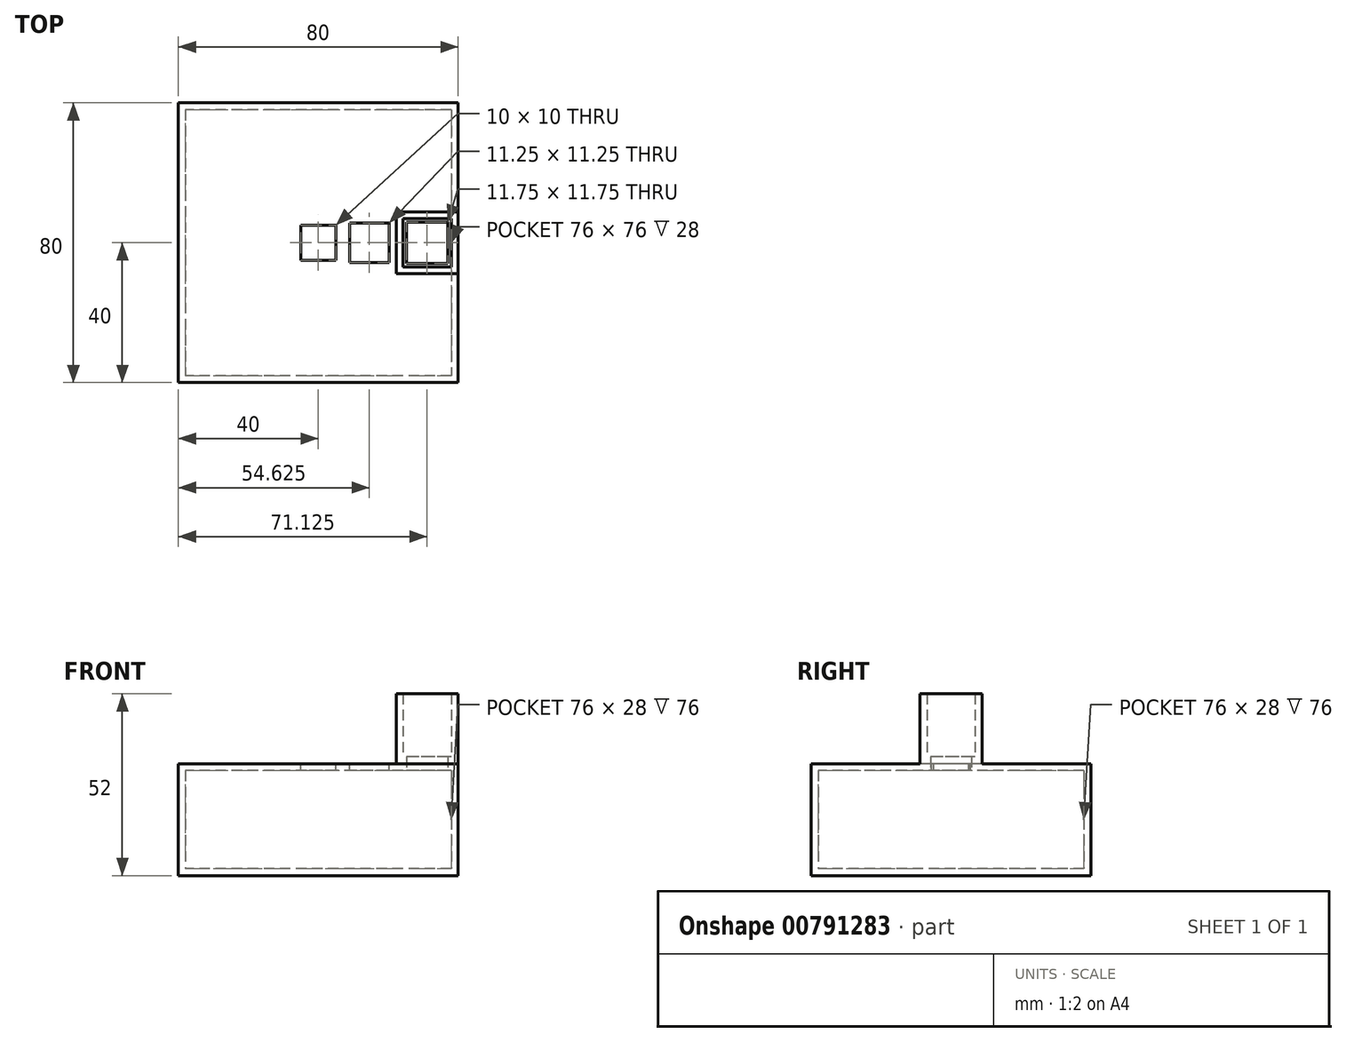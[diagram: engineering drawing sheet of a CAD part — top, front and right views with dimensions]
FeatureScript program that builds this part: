
annotation { "Feature Type Name" : "Feature", "Feature Type Description" : "" }
export const myFeature = defineFeature(function(context is Context, id is Id, definition is map)
    precondition{}
    {
        {
            var Q0;
            Q0=qCreatedBy(makeId("Top.planeOp"),FACE);
            var sketch = newSketch(context, id + "F0", { "sketchPlane" : qUnion([Q0])});
            skLineSegment(sketch, "E0.bottom", {"start": v(38, 38) * mm, "end": v(-38, 38) * mm});
            skLineSegment(sketch, "E0.top", {"start": v(38, -38) * mm, "end": v(-38, -38) * mm});
            skLineSegment(sketch, "E0.left", {"start": v(38, 38) * mm, "end": v(38, -38) * mm});
            skLineSegment(sketch, "E0.right", {"start": v(-38, 38) * mm, "end": v(-38, -38) * mm});
            skPoint(sketch, "E0.middle", {"position": v(0, 0) * mm});
            skLineSegment(sketch, "E1.bottom", {"start": v(40, 40) * mm, "end": v(-40, 40) * mm});
            skLineSegment(sketch, "E1.top", {"start": v(40, -40) * mm, "end": v(-40, -40) * mm});
            skLineSegment(sketch, "E1.left", {"start": v(40, 40) * mm, "end": v(40, -40) * mm});
            skLineSegment(sketch, "E1.right", {"start": v(-40, 40) * mm, "end": v(-40, -40) * mm});
            skLineSegment(sketch, "E2", {"start": v(-30, -38) * mm, "end": v(-30, -40) * mm});
            skLineSegment(sketch, "E3", {"start": v(-20, -38) * mm, "end": v(-20, -40) * mm});
            skLineSegment(sketch, "E4", {"start": v(-10, -38) * mm, "end": v(-10, -40) * mm});
            skLineSegment(sketch, "E5", {"start": v(3.33, -38) * mm, "end": v(3.33, -40) * mm});
            skLineSegment(sketch, "E6", {"start": v(10, -38) * mm, "end": v(10, -40) * mm});
            skLineSegment(sketch, "E7", {"start": v(20, -38) * mm, "end": v(20, -40) * mm});
            skLineSegment(sketch, "E8", {"start": v(30, -38) * mm, "end": v(30, -40) * mm});
            skLineSegment(sketch, "E9", {"start": v(40, -38) * mm, "end": v(40, -40) * mm});
            skLineSegment(sketch, "E10", {"start": v(-30, 40) * mm, "end": v(-30, 38) * mm});
            skLineSegment(sketch, "E11", {"start": v(-20, 40) * mm, "end": v(-20, 38) * mm});
            skLineSegment(sketch, "E12", {"start": v(-10, 40) * mm, "end": v(-10, 38) * mm});
            skLineSegment(sketch, "E13", {"start": v(10, 40) * mm, "end": v(10, 38) * mm});
            skLineSegment(sketch, "E14", {"start": v(20, 40) * mm, "end": v(20, 38) * mm});
            skLineSegment(sketch, "E15", {"start": v(30, 40) * mm, "end": v(30, 38) * mm});
            skLineSegment(sketch, "E16", {"start": v(-3.33, 40) * mm, "end": v(-3.33, 38) * mm});
            skLineSegment(sketch, "E17", {"start": v(3.33, 40) * mm, "end": v(3.33, 38) * mm});
            skLineSegment(sketch, "E18", {"start": v(-3.33, -38) * mm, "end": v(-3.33, -40) * mm});
            skSolve(sketch);
        }
        {
            var Q0;
            {var subQ3=sQuery(id+"F0.wireOp",EDGE,"E0.left");Q0=makeQuery(id+"F0.imprint","IMPRINT",FACE,{"disambiguationData":[TD([[makeQuery(id+"F0.imprint","IMPRINT",EDGE,{"derivedFrom":subQ3}),1.0]])]});}
            var Q1;
            {var subQ3=sQuery(id+"F0.wireOp",EDGE,"E0.right");Q1=makeQuery(id+"F0.imprint","IMPRINT",FACE,{"disambiguationData":[TD([[makeQuery(id+"F0.imprint","IMPRINT",EDGE,{"derivedFrom":subQ3}),-1.0]])]});}
            var Q2;
            {var subQ0=sQuery(id+"F0.wireOp",EDGE,"E10");Q2=makeQuery(id+"F0.imprint","IMPRINT",FACE,{"disambiguationData":[TD([[makeQuery(id+"F0.imprint","IMPRINT",EDGE,{"derivedFrom":subQ0}),1.0]])]});}
            var Q3;
            {var subQ0=sQuery(id+"F0.wireOp",EDGE,"E11");Q3=makeQuery(id+"F0.imprint","IMPRINT",FACE,{"disambiguationData":[TD([[makeQuery(id+"F0.imprint","IMPRINT",EDGE,{"derivedFrom":subQ0}),1.0]])]});}
            var Q4;
            {var subQ0=sQuery(id+"F0.wireOp",EDGE,"LYnKFG4Q-N3FC-TiNj-lwQl-nG8FpVbTfFSA");Q4=makeQuery(id+"F0.imprint","IMPRINT",FACE,{"disambiguationData":[TD([[makeQuery(id+"F0.imprint","IMPRINT",EDGE,{"derivedFrom":subQ0}),1.0]])]});}
            var Q5;
            {var subQ0=sQuery(id+"F0.wireOp",EDGE,"E12");Q5=makeQuery(id+"F0.imprint","IMPRINT",FACE,{"disambiguationData":[TD([[makeQuery(id+"F0.imprint","IMPRINT",EDGE,{"derivedFrom":subQ0}),1.0]])]});}
            var Q6;
            {var subQ0=sQuery(id+"F0.wireOp",EDGE,"KcaJ3uTN-FosF-TrTN-WjxN-LsLcIjeT56GG");Q6=makeQuery(id+"F0.imprint","IMPRINT",FACE,{"disambiguationData":[TD([[makeQuery(id+"F0.imprint","IMPRINT",EDGE,{"derivedFrom":subQ0}),1.0]])]});}
            var Q7;
            {var subQ0=sQuery(id+"F0.wireOp",EDGE,"E13");Q7=makeQuery(id+"F0.imprint","IMPRINT",FACE,{"disambiguationData":[TD([[makeQuery(id+"F0.imprint","IMPRINT",EDGE,{"derivedFrom":subQ0}),1.0]])]});}
            var Q8;
            {var subQ0=sQuery(id+"F0.wireOp",EDGE,"IDGARpov-2Fa3-cqG9-wXJu-bWtrQeb9REGT");Q8=makeQuery(id+"F0.imprint","IMPRINT",FACE,{"disambiguationData":[TD([[makeQuery(id+"F0.imprint","IMPRINT",EDGE,{"derivedFrom":subQ0}),1.0]])]});}
            var Q9;
            {var subQ0=sQuery(id+"F0.wireOp",EDGE,"E14");Q9=makeQuery(id+"F0.imprint","IMPRINT",FACE,{"disambiguationData":[TD([[makeQuery(id+"F0.imprint","IMPRINT",EDGE,{"derivedFrom":subQ0}),1.0]])]});}
            var Q10;
            {var subQ0=sQuery(id+"F0.wireOp",EDGE,"E8");Q10=makeQuery(id+"F0.imprint","IMPRINT",FACE,{"disambiguationData":[TD([[makeQuery(id+"F0.imprint","IMPRINT",EDGE,{"derivedFrom":subQ0}),1.0]])]});}
            var Q11;
            {var subQ0=sQuery(id+"F0.wireOp",EDGE,"E7");Q11=makeQuery(id+"F0.imprint","IMPRINT",FACE,{"disambiguationData":[TD([[makeQuery(id+"F0.imprint","IMPRINT",EDGE,{"derivedFrom":subQ0}),1.0]])]});}
            var Q12;
            {var subQ0=sQuery(id+"F0.wireOp",EDGE,"E6");Q12=makeQuery(id+"F0.imprint","IMPRINT",FACE,{"disambiguationData":[TD([[makeQuery(id+"F0.imprint","IMPRINT",EDGE,{"derivedFrom":subQ0}),1.0]])]});}
            var Q13;
            {var subQ0=sQuery(id+"F0.wireOp",EDGE,"EEPESouk-ZScJ-Ov81-QKdt-3qXRa8hrYlZT");Q13=makeQuery(id+"F0.imprint","IMPRINT",FACE,{"disambiguationData":[TD([[makeQuery(id+"F0.imprint","IMPRINT",EDGE,{"derivedFrom":subQ0}),1.0]])]});}
            var Q14;
            {var subQ0=sQuery(id+"F0.wireOp",EDGE,"E5");Q14=makeQuery(id+"F0.imprint","IMPRINT",FACE,{"disambiguationData":[TD([[makeQuery(id+"F0.imprint","IMPRINT",EDGE,{"derivedFrom":subQ0}),1.0]])]});}
            var Q15;
            {var subQ0=sQuery(id+"F0.wireOp",EDGE,"E4");Q15=makeQuery(id+"F0.imprint","IMPRINT",FACE,{"disambiguationData":[TD([[makeQuery(id+"F0.imprint","IMPRINT",EDGE,{"derivedFrom":subQ0}),1.0]])]});}
            var Q16;
            {var subQ0=sQuery(id+"F0.wireOp",EDGE,"E3");Q16=makeQuery(id+"F0.imprint","IMPRINT",FACE,{"disambiguationData":[TD([[makeQuery(id+"F0.imprint","IMPRINT",EDGE,{"derivedFrom":subQ0}),1.0]])]});}
            var Q17;
            {var subQ0=sQuery(id+"F0.wireOp",EDGE,"E2");Q17=makeQuery(id+"F0.imprint","IMPRINT",FACE,{"disambiguationData":[TD([[makeQuery(id+"F0.imprint","IMPRINT",EDGE,{"derivedFrom":subQ0}),1.0]])]});}
            var Q18;
            {var subQ0=sQuery(id+"F0.wireOp",EDGE,"E16");Q18=makeQuery(id+"F0.imprint","IMPRINT",FACE,{"disambiguationData":[TD([[makeQuery(id+"F0.imprint","IMPRINT",EDGE,{"derivedFrom":subQ0}),1.0]])]});}
            var Q19;
            {var subQ0=sQuery(id+"F0.wireOp",EDGE,"E13");Q19=makeQuery(id+"F0.imprint","IMPRINT",FACE,{"disambiguationData":[TD([[makeQuery(id+"F0.imprint","IMPRINT",EDGE,{"derivedFrom":subQ0}),-1.0]])]});}
            var Q20;
            {var subQ0=sQuery(id+"F0.wireOp",EDGE,"EEPESouk-ZScJ-Ov81-QKdt-3qXRa8hrYlZT");Q20=makeQuery(id+"F0.imprint","IMPRINT",FACE,{"disambiguationData":[TD([[makeQuery(id+"F0.imprint","IMPRINT",EDGE,{"derivedFrom":subQ0}),-1.0]])]});}
            var Q21;
            {var subQ0=sQuery(id+"F0.wireOp",EDGE,"E5");Q21=makeQuery(id+"F0.imprint","IMPRINT",FACE,{"disambiguationData":[TD([[makeQuery(id+"F0.imprint","IMPRINT",EDGE,{"derivedFrom":subQ0}),-1.0]])]});}
            extrude(context, id + "F1", {"entities" : qUnion([Q0, Q1, Q2, Q3, Q4, Q5, Q6, Q7, Q8, Q9, Q10, Q11, Q12, Q13, Q14, Q15, Q16, Q17, Q18, Q19, Q20, Q21]), "depth" : 30 * mm, "offsetDistance" : 25 * mm});
        }
        {
            var Q0;
            Q0=makeQuery(id+"F1.opExtrude","CAP_FACE",FACE,{"disambiguationData":[OSD([sQuery(id+"F0.wireOp",EDGE,"E0.bottom"),sQuery(id+"F0.wireOp",EDGE,"E0.top"),sQuery(id+"F0.wireOp",EDGE,"E0.left"),sQuery(id+"F0.wireOp",EDGE,"E0.right"),sQuery(id+"F0.wireOp",EDGE,"E1.bottom"),sQuery(id+"F0.wireOp",EDGE,"E1.top"),sQuery(id+"F0.wireOp",EDGE,"E1.left"),sQuery(id+"F0.wireOp",EDGE,"E1.right")])],"isStart":false});
            var sketch = newSketch(context, id + "F2", { "sketchPlane" : qUnion([Q0])});
            skLineSegment(sketch, "E19.bottom", {"start": v(5, 5) * mm, "end": v(-5, 5) * mm});
            skLineSegment(sketch, "E19.top", {"start": v(5, -5) * mm, "end": v(-5, -5) * mm});
            skLineSegment(sketch, "E19.left", {"start": v(5, 5) * mm, "end": v(5, -5) * mm});
            skLineSegment(sketch, "E19.right", {"start": v(-5, 5) * mm, "end": v(-5, -5) * mm});
            skPoint(sketch, "E19.middle", {"position": v(0, 0) * mm});
            skLineSegment(sketch, "E20.bottom", {"start": v(20.25, 5.63) * mm, "end": v(9, 5.63) * mm});
            skLineSegment(sketch, "E20.top", {"start": v(20.25, -5.62) * mm, "end": v(9, -5.62) * mm});
            skLineSegment(sketch, "E20.left", {"start": v(20.25, 5.63) * mm, "end": v(20.25, -5.62) * mm});
            skLineSegment(sketch, "E20.right", {"start": v(9, 5.63) * mm, "end": v(9, -5.62) * mm});
            skPoint(sketch, "E20.middle", {"position": v(14.62, 0) * mm});
            skLineSegment(sketch, "E21.bottom", {"start": v(40, 8.88) * mm, "end": v(22.25, 8.88) * mm});
            skLineSegment(sketch, "E21.top", {"start": v(40, -8.87) * mm, "end": v(22.25, -8.87) * mm});
            skLineSegment(sketch, "E21.left", {"start": v(40, 8.88) * mm, "end": v(40, -8.87) * mm});
            skLineSegment(sketch, "E21.right", {"start": v(22.25, 8.88) * mm, "end": v(22.25, -8.87) * mm});
            skPoint(sketch, "E21.middle", {"position": v(31.12, 0) * mm});
            skLineSegment(sketch, "E22.bottom", {"start": v(38, 6.87) * mm, "end": v(24.25, 6.88) * mm});
            skLineSegment(sketch, "E22.top", {"start": v(38, -6.87) * mm, "end": v(24.25, -6.87) * mm});
            skLineSegment(sketch, "E22.left", {"start": v(38, 6.87) * mm, "end": v(38, -6.87) * mm});
            skLineSegment(sketch, "E22.right", {"start": v(24.25, 6.88) * mm, "end": v(24.25, -6.87) * mm});
            skLineSegment(sketch, "E23.bottom", {"start": v(37, 5.87) * mm, "end": v(25.25, 5.88) * mm});
            skLineSegment(sketch, "E23.top", {"start": v(37, -5.87) * mm, "end": v(25.25, -5.87) * mm});
            skLineSegment(sketch, "E23.left", {"start": v(37, 5.87) * mm, "end": v(37, -5.87) * mm});
            skLineSegment(sketch, "E23.right", {"start": v(25.25, 5.88) * mm, "end": v(25.25, -5.87) * mm});
            skSolve(sketch);
        }
        {
            var Q0;
            Q0=makeQuery(id+"F2.imprint","IMPRINT",FACE,{"disambiguationData":[TD([[makeQuery(id+"F2.imprint","IMPRINT",EDGE,{"derivedFrom":sQuery(id+"F2.wireOp",EDGE,"E19.bottom")}),-1.0]])]});
            var Q1;
            Q1=makeQuery(id+"F2.imprint","IMPRINT",FACE,{"disambiguationData":[TD([[makeQuery(id+"F2.imprint","IMPRINT",EDGE,{"derivedFrom":sQuery(id+"F2.wireOp",EDGE,"E21.bottom")}),1.0]])]});
            var Q2;
            {var subQ0=sQuery(id+"F2.wireOp",EDGE,"E21.right");Q2=makeQuery(id+"F2.imprint","IMPRINT",FACE,{"disambiguationData":[TD([[makeQuery(id+"F2.imprint","IMPRINT",EDGE,{"derivedFrom":subQ0}),1.0]])]});}
            extrude(context, id + "F3", {"entities" : qUnion([Q0, Q1, Q2]), "depth" : -2 * mm, "offsetDistance" : 25 * mm});
        }
        {
            var Q0;
            Q0=makeQuery(id+"F2.imprint","IMPRINT",FACE,{"disambiguationData":[TD([[makeQuery(id+"F2.imprint","IMPRINT",EDGE,{"derivedFrom":sQuery(id+"F2.wireOp",EDGE,"E21.bottom")}),1.0]])]});
            var Q1;
            {var subQ0=sQuery(id+"F2.wireOp",EDGE,"E21.right");Q1=makeQuery(id+"F2.imprint","IMPRINT",FACE,{"disambiguationData":[TD([[makeQuery(id+"F2.imprint","IMPRINT",EDGE,{"derivedFrom":subQ0}),1.0]])]});}
            extrude(context, id + "F4", {"entities" : qUnion([Q0, Q1]), "depth" : 20 * mm, "offsetDistance" : 25 * mm});
        }
        {
            var Q0;
            {var subQ12=sQuery(id+"F0.wireOp",EDGE,"E0.left");Q0=makeQuery(id+"F0.imprint","IMPRINT",FACE,{"disambiguationData":[TD([[makeQuery(id+"F0.imprint","IMPRINT",EDGE,{"derivedFrom":subQ12}),-1.0]])]});}
            var Q1;
            {var subQ0=sQuery(id+"F0.wireOp",EDGE,"E10");Q1=makeQuery(id+"F0.imprint","IMPRINT",FACE,{"disambiguationData":[TD([[makeQuery(id+"F0.imprint","IMPRINT",EDGE,{"derivedFrom":subQ0}),1.0]])]});}
            var Q2;
            {var subQ0=sQuery(id+"F0.wireOp",EDGE,"LYnKFG4Q-N3FC-TiNj-lwQl-nG8FpVbTfFSA");Q2=makeQuery(id+"F0.imprint","IMPRINT",FACE,{"disambiguationData":[TD([[makeQuery(id+"F0.imprint","IMPRINT",EDGE,{"derivedFrom":subQ0}),1.0]])]});}
            var Q3;
            {var subQ0=sQuery(id+"F0.wireOp",EDGE,"E14");Q3=makeQuery(id+"F0.imprint","IMPRINT",FACE,{"disambiguationData":[TD([[makeQuery(id+"F0.imprint","IMPRINT",EDGE,{"derivedFrom":subQ0}),1.0]])]});}
            var Q4;
            {var subQ0=sQuery(id+"F0.wireOp",EDGE,"EEPESouk-ZScJ-Ov81-QKdt-3qXRa8hrYlZT");Q4=makeQuery(id+"F0.imprint","IMPRINT",FACE,{"disambiguationData":[TD([[makeQuery(id+"F0.imprint","IMPRINT",EDGE,{"derivedFrom":subQ0}),-1.0]])]});}
            var Q5;
            {var subQ0=sQuery(id+"F0.wireOp",EDGE,"E4");Q5=makeQuery(id+"F0.imprint","IMPRINT",FACE,{"disambiguationData":[TD([[makeQuery(id+"F0.imprint","IMPRINT",EDGE,{"derivedFrom":subQ0}),1.0]])]});}
            var Q6;
            {var subQ0=sQuery(id+"F0.wireOp",EDGE,"E2");Q6=makeQuery(id+"F0.imprint","IMPRINT",FACE,{"disambiguationData":[TD([[makeQuery(id+"F0.imprint","IMPRINT",EDGE,{"derivedFrom":subQ0}),1.0]])]});}
            var Q7;
            {var subQ0=sQuery(id+"F0.wireOp",EDGE,"E5");Q7=makeQuery(id+"F0.imprint","IMPRINT",FACE,{"disambiguationData":[TD([[makeQuery(id+"F0.imprint","IMPRINT",EDGE,{"derivedFrom":subQ0}),1.0]])]});}
            var Q8;
            {var subQ0=sQuery(id+"F0.wireOp",EDGE,"E7");Q8=makeQuery(id+"F0.imprint","IMPRINT",FACE,{"disambiguationData":[TD([[makeQuery(id+"F0.imprint","IMPRINT",EDGE,{"derivedFrom":subQ0}),1.0]])]});}
            var Q9;
            {var subQ0=sQuery(id+"F0.wireOp",EDGE,"E12");Q9=makeQuery(id+"F0.imprint","IMPRINT",FACE,{"disambiguationData":[TD([[makeQuery(id+"F0.imprint","IMPRINT",EDGE,{"derivedFrom":subQ0}),1.0]])]});}
            var Q10;
            {var subQ0=sQuery(id+"F0.wireOp",EDGE,"E13");Q10=makeQuery(id+"F0.imprint","IMPRINT",FACE,{"disambiguationData":[TD([[makeQuery(id+"F0.imprint","IMPRINT",EDGE,{"derivedFrom":subQ0}),-1.0]])]});}
            extrude(context, id + "F5", {"entities" : qUnion([Q0, Q1, Q2, Q3, Q4, Q5, Q6, Q7, Q8, Q9, Q10]), "oppositeDirection" : true, "depth" : 2 * mm, "offsetDistance" : 25 * mm});
        }
        {
            var Q0;
            Q0=makeQuery(id+"F2.imprint","IMPRINT",FACE,{"disambiguationData":[TD([[makeQuery(id+"F2.imprint","IMPRINT",EDGE,{"derivedFrom":sQuery(id+"F2.wireOp",EDGE,"E22.bottom")}),1.0]])]});
            extrude(context, id + "F6", {"entities" : qUnion([Q0]), "operationType" : NewBodyOperationType.ADD, "endBound" : BoundingType.SYMMETRIC, "depth" : 4 * mm, "offsetDistance" : 25 * mm});
        }
        {
            var Q0;
            {var subQ0=sQuery(id+"F0.wireOp",EDGE,"E0.right");Q0=makeQuery(id+"F0.imprint","IMPRINT",FACE,{"disambiguationData":[TD([[makeQuery(id+"F0.imprint","IMPRINT",EDGE,{"derivedFrom":subQ0}),-1.0]])]});}
            var Q1;
            {var subQ0=sQuery(id+"F0.wireOp",EDGE,"E11");Q1=makeQuery(id+"F0.imprint","IMPRINT",FACE,{"disambiguationData":[TD([[makeQuery(id+"F0.imprint","IMPRINT",EDGE,{"derivedFrom":subQ0}),1.0]])]});}
            var Q2;
            {var subQ0=sQuery(id+"F0.wireOp",EDGE,"E16");Q2=makeQuery(id+"F0.imprint","IMPRINT",FACE,{"disambiguationData":[TD([[makeQuery(id+"F0.imprint","IMPRINT",EDGE,{"derivedFrom":subQ0}),1.0]])]});}
            var Q3;
            {var subQ0=sQuery(id+"F0.wireOp",EDGE,"E13");Q3=makeQuery(id+"F0.imprint","IMPRINT",FACE,{"disambiguationData":[TD([[makeQuery(id+"F0.imprint","IMPRINT",EDGE,{"derivedFrom":subQ0}),1.0]])]});}
            var Q4;
            {var subQ0=sQuery(id+"F0.wireOp",EDGE,"E0.left");Q4=makeQuery(id+"F0.imprint","IMPRINT",FACE,{"disambiguationData":[TD([[makeQuery(id+"F0.imprint","IMPRINT",EDGE,{"derivedFrom":subQ0}),1.0]])]});}
            var Q5;
            {var subQ0=sQuery(id+"F0.wireOp",EDGE,"E6");Q5=makeQuery(id+"F0.imprint","IMPRINT",FACE,{"disambiguationData":[TD([[makeQuery(id+"F0.imprint","IMPRINT",EDGE,{"derivedFrom":subQ0}),1.0]])]});}
            var Q6;
            {var subQ0=sQuery(id+"F0.wireOp",EDGE,"E5");Q6=makeQuery(id+"F0.imprint","IMPRINT",FACE,{"disambiguationData":[TD([[makeQuery(id+"F0.imprint","IMPRINT",EDGE,{"derivedFrom":subQ0}),-1.0]])]});}
            var Q7;
            {var subQ0=sQuery(id+"F0.wireOp",EDGE,"E3");Q7=makeQuery(id+"F0.imprint","IMPRINT",FACE,{"disambiguationData":[TD([[makeQuery(id+"F0.imprint","IMPRINT",EDGE,{"derivedFrom":subQ0}),1.0]])]});}
            extrude(context, id + "F7", {"entities" : qUnion([Q0, Q1, Q2, Q3, Q4, Q5, Q6, Q7]), "operationType" : NewBodyOperationType.ADD, "oppositeDirection" : true, "depth" : 2 * mm, "offsetDistance" : 25 * mm});
        }
    });
